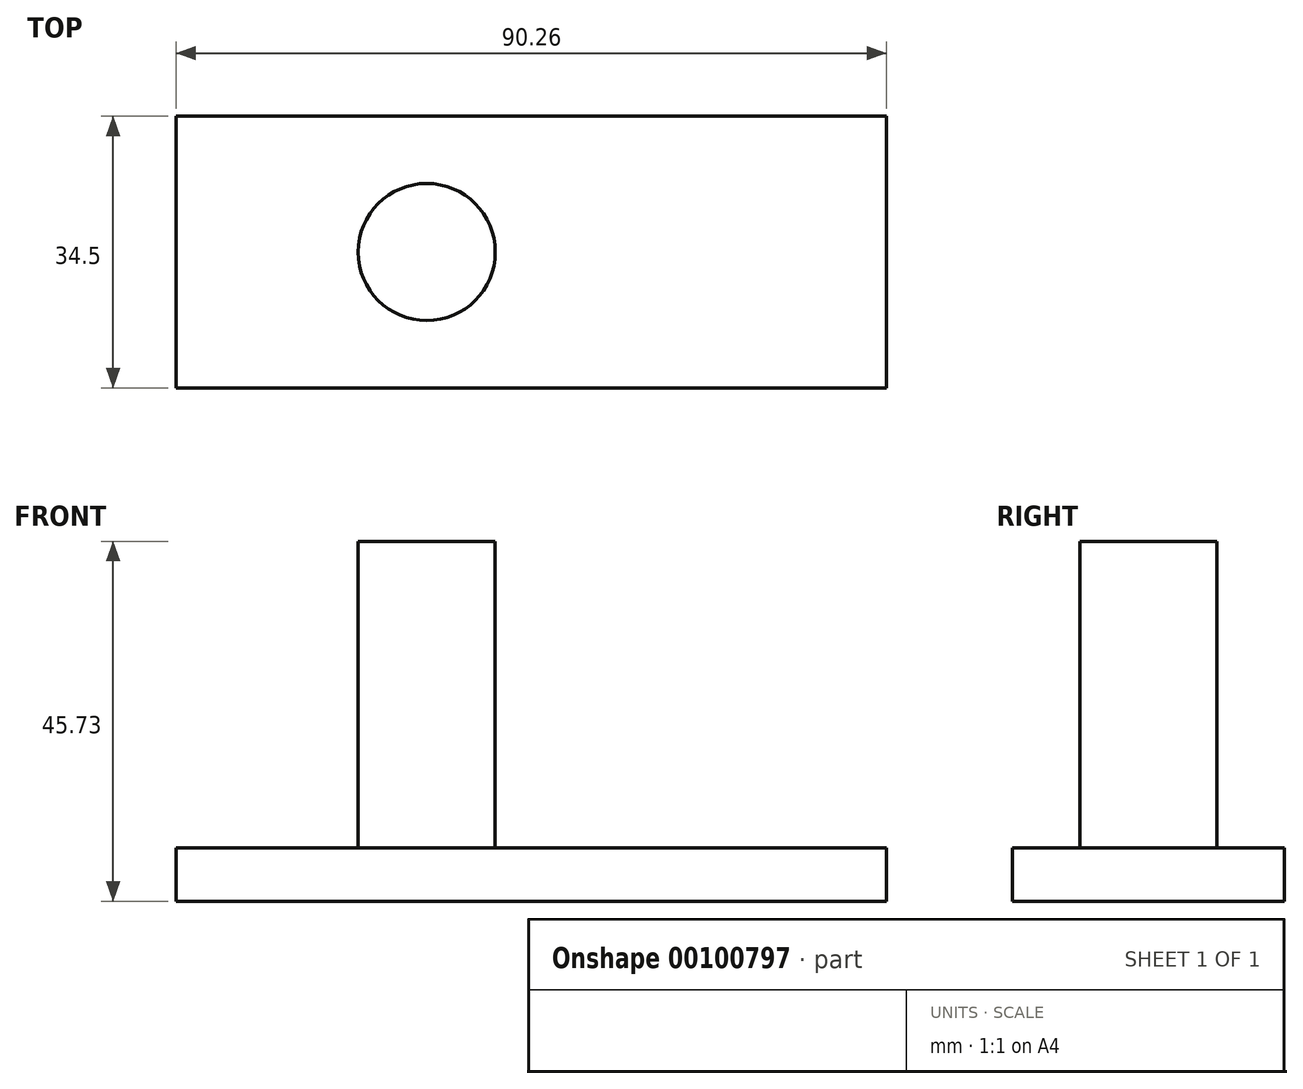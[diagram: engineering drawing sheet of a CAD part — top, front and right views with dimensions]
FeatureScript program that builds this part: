
annotation { "Feature Type Name" : "Feature", "Feature Type Description" : "" }
export const myFeature = defineFeature(function(context is Context, id is Id, definition is map)
    precondition{}
    {
        {
            var Q0;
            Q0=qCreatedBy(makeId("Front.planeOp"),FACE);
            var sketch = newSketch(context, id + "F0", { "sketchPlane" : qUnion([Q0])});
            skLineSegment(sketch, "E0.bottom", {"start": v(0, 0) * mm, "end": v(-8.7, 0) * mm});
            skLineSegment(sketch, "E0.top", {"start": v(0, 38.97) * mm, "end": v(-8.7, 38.97) * mm});
            skLineSegment(sketch, "E0.left", {"start": v(0, 0) * mm, "end": v(0, 38.97) * mm});
            skLineSegment(sketch, "E0.right", {"start": v(-8.7, 0) * mm, "end": v(-8.7, 38.97) * mm});
            skSolve(sketch);
        }
        {
            var Q0;
            Q0=makeQuery(id+"F0.imprint","IMPRINT",FACE,{"disambiguationData":[TD([[makeQuery(id+"F0.imprint","IMPRINT",EDGE,{"derivedFrom":sQuery(id+"F0.wireOp",EDGE,"E0.bottom")}),-1.0]])]});
            var Q1;
            Q1=sQuery(id+"F0.wireOp",EDGE,"E0.left");
            revolve(context, id + "F1", {"entities" : qUnion([Q0]), "axis" : qUnion([Q1]), "revolveType" : RevolveType.FULL});
        }
        {
            var Q0;
            Q0=qCreatedBy(makeId("Top.planeOp"),FACE);
            var sketch = newSketch(context, id + "F2", { "sketchPlane" : qUnion([Q0])});
            skLineSegment(sketch, "E1.bottom", {"start": v(-31.84, 17.25) * mm, "end": v(58.42, 17.25) * mm});
            skLineSegment(sketch, "E1.top", {"start": v(-31.84, -17.25) * mm, "end": v(58.42, -17.25) * mm});
            skLineSegment(sketch, "E1.left", {"start": v(-31.84, 17.25) * mm, "end": v(-31.84, -17.25) * mm});
            skLineSegment(sketch, "E1.right", {"start": v(58.42, 17.25) * mm, "end": v(58.42, -17.25) * mm});
            skPoint(sketch, "E1.middle", {"position": v(13.3, 0) * mm});
            skSolve(sketch);
        }
        {
            var Q0;
            Q0 = qSketchRegion(id + "F2", true);
            extrude(context, id + "F3", {"entities" : qUnion([Q0]), "operationType" : NewBodyOperationType.ADD, "oppositeDirection" : true, "depth" : 6.76 * mm});
        }
    });
